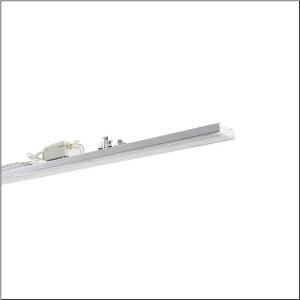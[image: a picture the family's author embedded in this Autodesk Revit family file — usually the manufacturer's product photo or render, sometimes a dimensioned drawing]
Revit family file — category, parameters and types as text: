
# Revit family: licross_11_recessed_mo_51te12dv4fxg3c
name_source: partatom
category: Lighting Fixtures
units: mm (PartAtom-declared; Revit-internal decimal feet)

## family parameters
Cut with Voids When Loaded = No
Host = Face
Light Source = No
Part Type = Normal
Room Calculation Point = No
Round Connector Dimension = Use Diameter
Shared = No

## types (1)
- --- (1 x LED, 1010 lm, 5.5 W, 4000K)
    Apparent Load = 6 VA
    CIE Flux Codes = 67 92 99 100 100
    Color Rendering = 80
    Color Temperature = 4000K
    Default Elevation = 1800 mm
    Description = Licross 11 Recessed MO, luminaire insert, of sheet steel, galvanised, coil coated, white, length: 2.250mm, width: 66mm, height: 67mm, LED rated luminous flux: 15.360lm, light colour: 840, SDCM (Standard Deviation of Colour Matching)MacAdam ≤ 2 SDCM (initial), control gear: DALI 2 (for two DALI lines), with plug, 6-pole, with phase selection, for trunking rail, 14-core, mains connection: 220..240V, AC, 50/60Hz, rated input power: 88W, for trunking rail, 14-core, internal wiring halogen-free, for emergency light function, converter,control gear: single battery element, battery: LiFePO4, 9Ah, primary optical cover: cover, of PMMA, light emission: direct distribution, primary light characteristic: symmetric, protection rating (complete): IP54, insulation class (complete): insulation class I (protective earthing), certification: CE, UKCA, protection symbol: D if used in an environment with non-conductive dust loads with corresponding accessories, impact resistance: IK06, permissible ambient temperature for indoor applications: +5..+35°C, standard: EN 60598-2-22, LABS conformity tested according to VDMA 24364:2018-05, reducing of maximum allowable ambient temperature of 5°C with ceiling mounting, corresponds to IFS (International Featured Standards) requirements for safety and quality in the food industry, The light source and the operating device comply with the requirements of the Ecodesign Regulation (EU) 2019/2020 and are replaceable in accordance with this regulation, packaging unit: 1 piece
    Height = 58 mm
    Lamp = 1 x LED
    Lamp Light Flux = 1010 lm
    Lamp Power = 5.5 W
    Lamp count = 1
    Length = 2250 mm
    Luminous efficacy = 184 lm/W
    Manufacturer = Siteco
    ModVariant = No
    Model = 51TE12DV4FXG3C
    Mounting Place = Ceiling
    Mounting Type = Pendant
    Number of Poles = 1
    OnlyDefault = Yes
    Power Factor = 1
    Product Name = Licross 11 Recessed MO
    Product group = luminaire insert | ceiling pendant
    ProductGroupID = 901
    Protection Class = Protection class I
    Protection Degree = IP 54
    RLX_Detail_Level = 1
    RLX_Emergency_Light_Flux = 0 lm
    RLX_Emergency_Type = 0
    RLX_Emergency_Type_DB = No
    RlxData = <blob elided: 30137 chars, md5=15e7f6d7>
    Socket = socket
    Standby Power = 0 W
    System Light Flux = 1010 lm
    System Power = 6 W
    Type Comments = : emergency light operation: 3 h
    Type Image = l_1296930.jpg
    URL = http://relux.com
    VarID = @adj_091575
    Voltage = 0 V
    Weight = 0.00 kg
    Width = 66 mm

## geometry (parser evidence)
native form markers: Blend x4, Sweep x10
no freeform markers — native parametric forms only
